# Revit family: ECJN
name_source: partatom
category: Lighting Fixtures
revit_build: Autodesk Revit 2014 (Build: 20130308_1515(x64)
units: mm (PartAtom-declared; Revit-internal decimal feet)

## types (1)
- ECJN
    Apparent Load = 75 VA
    Assembly Code = D5020200
    Color Filter = 16777215
    Connector Description = Lighting Connector
    Default Elevation = 1219.2 mm  [stored 4 ft]
    Description = The Eclipse Junior is a compact wellglass that incorporates the low maintenance features of the Eclipse II. Its low profile design and range of mounting options, offers an all round lighting solution in areas of limited space. The junior is available with a range up lamp types up to 150W and is suitable for use at low temperatures (-30°C).
    Dimming Lamp Color Temperature Shift = <None>
    Emit Shape Visible in Rendering = No
    Emit from Circle Diameter = 50 mm  [stored 0.164042 ft]
    Features = Compact size and low weight.
Easy access for wiring and control gear.
Unrestricted breathing gear enclosure removes the need for special glands or cable.
Corrosion resistant.
Excellent light distribution.
Suitable for a wide range of ambient temperatures from -30˚C to +55˚C, dependant on lamp type and wattage.
Option available for Zone 22 combustable dust environments.
GOST-R and CEPEL Approved.
    Fixture distribution = Direct
    Glass = Hubbell - Glass
    Height = 535 mm
    Housing Material = Paint - Hubbell - White Texture
    IP Rating = IP66/67
    Inner Length = 200 mm  [stored 0.656168 ft]
    Lamp = LED
    Length = 245 mm  [stored 0.803806 ft]
    Load Classification = Lighting
    Manufacturer = Chalmit
    Model = ECJN
    Mounting = Paint - Hubbell - Light Silver
    Photometric Web File = CHL_ECJN_050_HS.ies
    Power Factor = 1
    Product Documentation Link = https://hubbellcdn.com
    Product Link = https://www.hubbell.com
    Reflector Finish = Hubbell - White Glass
    Tilt Angle = 90.00°
    URL = https://www.hubbell.com
    Voltage = 120 V
    Warranty = 5 years Warranty
    Wattage Comments = 75W
    Watts = 75 W
    Width = 280 mm  [stored 0.918635 ft]
    Wings = Paint - Hubbell - Light Silver

note: [stored X ft] marks values corroborated as IEEE doubles in the binary element streams (Revit-internal decimal feet)

## geometry (parser evidence)
native form markers: Sweep x3
no freeform markers — native parametric forms only
